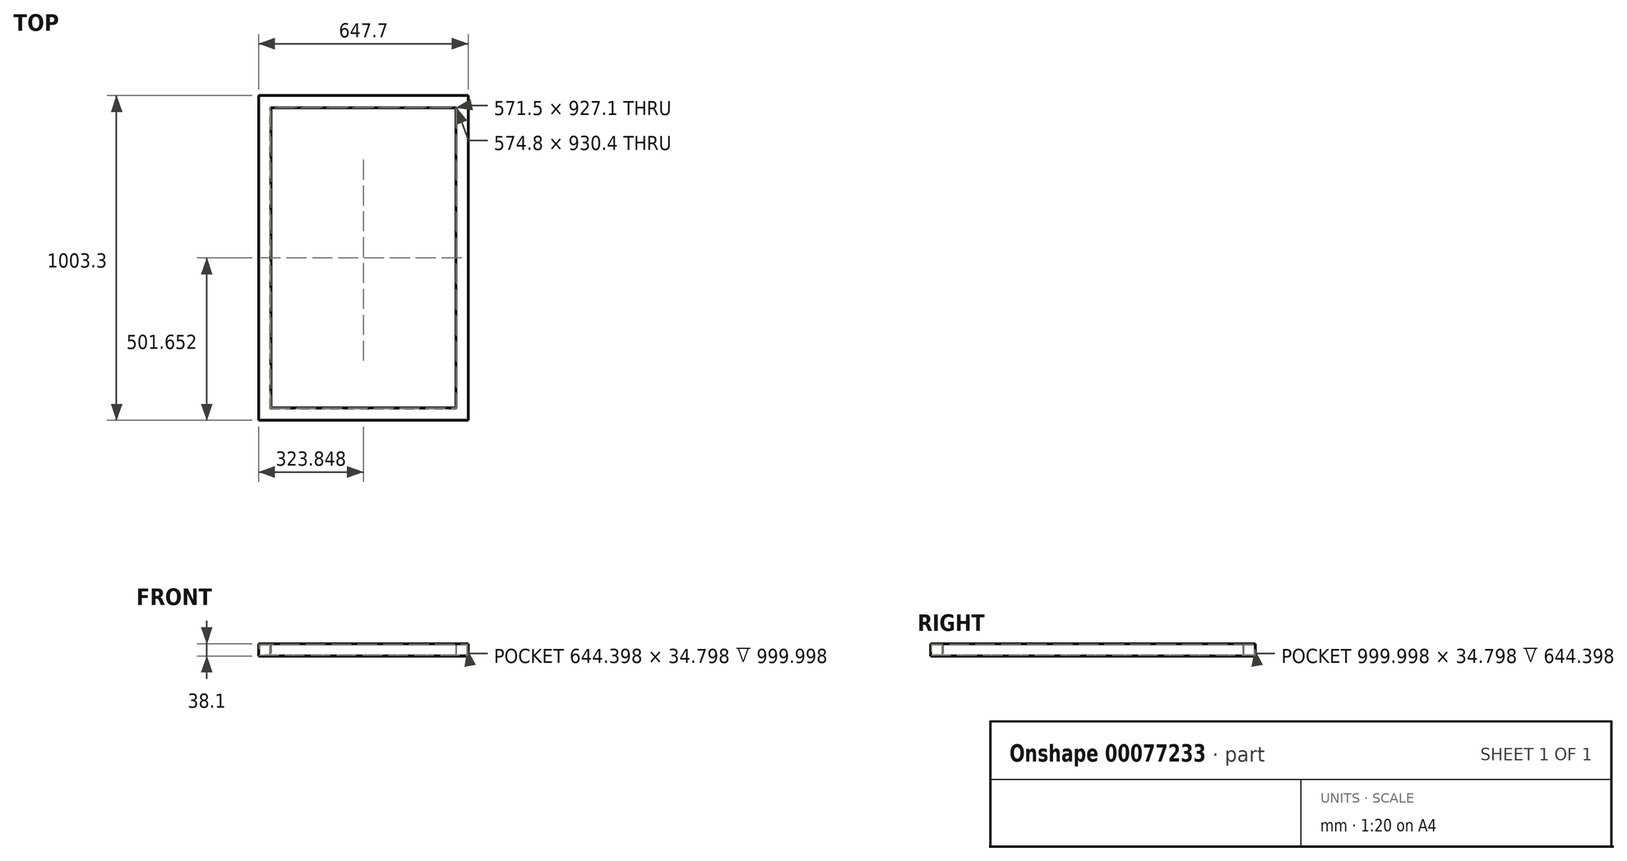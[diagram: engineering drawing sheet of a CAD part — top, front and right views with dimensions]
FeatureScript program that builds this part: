
annotation { "Feature Type Name" : "Feature", "Feature Type Description" : "" }
export const myFeature = defineFeature(function(context is Context, id is Id, definition is map)
    precondition{}
    {
        {
            var Q0;
            Q0=qCreatedBy(makeId("Top.planeOp"),FACE);
            var sketch = newSketch(context, id + "F0", { "sketchPlane" : qUnion([Q0])});
            skLineSegment(sketch, "E0", {"start": v(-90.31, 507.3) * mm, "end": v(-90.31, -496) * mm});
            skLineSegment(sketch, "E1", {"start": v(-90.31, -496) * mm, "end": v(-52.21, -457.9) * mm});
            skLineSegment(sketch, "E2", {"start": v(-52.21, -457.9) * mm, "end": v(-52.21, 469.2) * mm});
            skLineSegment(sketch, "E3", {"start": v(-52.21, 469.2) * mm, "end": v(-90.31, 507.3) * mm});
            skLineSegment(sketch, "E4", {"start": v(-90.31, 507.3) * mm, "end": v(557.39, 507.3) * mm});
            skLineSegment(sketch, "E5", {"start": v(-52.21, 469.2) * mm, "end": v(519.29, 469.2) * mm});
            skLineSegment(sketch, "E6", {"start": v(519.29, 469.2) * mm, "end": v(557.39, 507.3) * mm});
            skLineSegment(sketch, "E7", {"start": v(519.29, 469.2) * mm, "end": v(519.29, -457.9) * mm});
            skLineSegment(sketch, "E8", {"start": v(557.39, 507.3) * mm, "end": v(557.39, -496) * mm});
            skLineSegment(sketch, "E9", {"start": v(557.39, -496) * mm, "end": v(519.29, -457.9) * mm});
            skLineSegment(sketch, "E10", {"start": v(-90.31, -496) * mm, "end": v(557.39, -496) * mm});
            skLineSegment(sketch, "E11", {"start": v(519.29, -457.9) * mm, "end": v(-52.21, -457.9) * mm});
            skSolve(sketch);
        }
        {
            var Q0;
            Q0=makeQuery(id+"F0.imprint","IMPRINT",FACE,{"disambiguationData":[TD([[makeQuery(id+"F0.imprint","IMPRINT",EDGE,{"derivedFrom":sQuery(id+"F0.wireOp",EDGE,"E0")}),1.0]])]});
            extrude(context, id + "F1", {"entities" : qUnion([Q0]), "endBound" : BoundingType.SYMMETRIC, "depth" : 38.1 * mm});
        }
        {
            var Q0;
            Q0=qCreatedBy(makeId("Front.planeOp"),FACE);
            var sketch = newSketch(context, id + "F2", { "sketchPlane" : qUnion([Q0])});
            skLineSegment(sketch, "E12.bottom", {"start": v(-88.66, 17.4) * mm, "end": v(-53.86, 17.4) * mm});
            skLineSegment(sketch, "E12.top", {"start": v(-88.66, -17.4) * mm, "end": v(-53.86, -17.4) * mm});
            skLineSegment(sketch, "E12.left", {"start": v(-88.66, 17.4) * mm, "end": v(-88.66, -17.4) * mm});
            skLineSegment(sketch, "E12.right", {"start": v(-53.86, 17.4) * mm, "end": v(-53.86, -17.4) * mm});
            skSolve(sketch);
        }
        {
            var Q0;
            Q0 = qSketchRegion(id + "F2", true);
            extrude(context, id + "F3", {"entities" : qUnion([Q0]), "operationType" : NewBodyOperationType.REMOVE, "endBound" : BoundingType.SYMMETRIC, "depth" : 1016 * mm});
        }
        {
            var Q0;
            Q0=makeQuery(id+"F0.imprint","IMPRINT",FACE,{"disambiguationData":[TD([[makeQuery(id+"F0.imprint","IMPRINT",EDGE,{"derivedFrom":sQuery(id+"F0.wireOp",EDGE,"E3")}),-1.0]])]});
            extrude(context, id + "F4", {"entities" : qUnion([Q0]), "operationType" : NewBodyOperationType.ADD, "endBound" : BoundingType.SYMMETRIC, "depth" : 38.1 * mm});
        }
        {
            var Q0;
            Q0=qCreatedBy(makeId("Right.planeOp"),FACE);
            var sketch = newSketch(context, id + "F5", { "sketchPlane" : qUnion([Q0])});
            skLineSegment(sketch, "E13.bottom", {"start": v(505.65, 17.4) * mm, "end": v(470.85, 17.4) * mm});
            skLineSegment(sketch, "E13.top", {"start": v(505.65, -17.4) * mm, "end": v(470.85, -17.4) * mm});
            skLineSegment(sketch, "E13.left", {"start": v(505.65, 17.4) * mm, "end": v(505.65, -17.4) * mm});
            skLineSegment(sketch, "E13.right", {"start": v(470.85, 17.4) * mm, "end": v(470.85, -17.4) * mm});
            skPoint(sketch, "E13.middle", {"position": v(488.25, 0) * mm});
            skSolve(sketch);
        }
        {
            var Q0;
            Q0 = qSketchRegion(id + "F5", true);
            var Q1;
            Q1=makeQuery(id+"F1.opExtrude","SWEPT_FACE",FACE,{"disambiguationData":[OSD([sQuery(id+"F0.wireOp",EDGE,"E0")])]});
            var Q2;
            Q2=makeQuery(id+"F4.opExtrude","SWEPT_FACE",FACE,{"disambiguationData":[OSD([sQuery(id+"F0.wireOp",EDGE,"E4")])]});
            extrude(context, id + "F6", {"entities" : qUnion([Q0]), "operationType" : NewBodyOperationType.REMOVE, "endBound" : BoundingType.UP_TO_NEXT, "endBoundEntityFace" : qUnion([Q1]), "depth" : 610.27 * mm, "hasSecondDirection" : true, "secondDirectionBound" : SecondDirectionBoundingType.UP_TO_NEXT, "secondDirectionOppositeDirection" : true, "secondDirectionBoundEntityFace" : qUnion([Q2]), "secondDirectionDepth" : 25.4 * mm});
        }
        {
            var Q0;
            Q0=makeQuery(id+"F0.imprint","IMPRINT",FACE,{"disambiguationData":[TD([[makeQuery(id+"F0.imprint","IMPRINT",EDGE,{"derivedFrom":sQuery(id+"F0.wireOp",EDGE,"E6")}),-1.0]])]});
            var Q1;
            Q1 = qSketchRegion(id + "F8", true);
            extrude(context, id + "F7", {"entities" : qUnion([Q0, Q1]), "operationType" : NewBodyOperationType.ADD, "endBound" : BoundingType.SYMMETRIC, "depth" : 38.1 * mm});
        }
        {
            var Q0;
            Q0=qCreatedBy(makeId("Front.planeOp"),FACE);
            var sketch = newSketch(context, id + "F8", { "sketchPlane" : qUnion([Q0])});
            skLineSegment(sketch, "E14.bottom", {"start": v(555.74, 17.4) * mm, "end": v(520.94, 17.4) * mm});
            skLineSegment(sketch, "E14.top", {"start": v(555.74, -17.4) * mm, "end": v(520.94, -17.4) * mm});
            skLineSegment(sketch, "E14.left", {"start": v(555.74, 17.4) * mm, "end": v(555.74, -17.4) * mm});
            skLineSegment(sketch, "E14.right", {"start": v(520.94, 17.4) * mm, "end": v(520.94, -17.4) * mm});
            skSolve(sketch);
        }
        {
            var Q0;
            Q0 = qSketchRegion(id + "F8", true);
            var Q1;
            Q1=makeQuery(id+"F4.opExtrude","SWEPT_FACE",FACE,{"disambiguationData":[OSD([sQuery(id+"F0.wireOp",EDGE,"E5")])]});
            var Q2;
            Q2=makeQuery(id+"F1.opExtrude","SWEPT_BODY",BODY,{"disambiguationData":[OSD([sQuery(id+"F0.wireOp",EDGE,"E0"),sQuery(id+"F0.wireOp",EDGE,"E1"),sQuery(id+"F0.wireOp",EDGE,"E2"),sQuery(id+"F0.wireOp",EDGE,"E3")])]});
            var Q3;
            Q3=makeQuery(id+"F1.opExtrude","SWEPT_BODY",BODY,{"disambiguationData":[OSD([sQuery(id+"F0.wireOp",EDGE,"E0"),sQuery(id+"F0.wireOp",EDGE,"E1"),sQuery(id+"F0.wireOp",EDGE,"E2"),sQuery(id+"F0.wireOp",EDGE,"E3")])]});
            extrude(context, id + "F9", {"entities" : qUnion([Q0]), "operationType" : NewBodyOperationType.REMOVE, "endBound" : BoundingType.UP_TO_BODY, "oppositeDirection" : true, "endBoundEntityFace" : qUnion([Q1]), "endBoundEntityBody" : qUnion([Q2]), "depth" : 25.4 * mm, "hasSecondDirection" : true, "secondDirectionBound" : SecondDirectionBoundingType.UP_TO_BODY, "secondDirectionOppositeDirection" : false, "secondDirectionBoundEntityBody" : qUnion([Q3]), "secondDirectionDepth" : 25.4 * mm});
        }
        {
            var Q0;
            Q0=makeQuery(id+"F0.imprint","IMPRINT",FACE,{"disambiguationData":[TD([[makeQuery(id+"F0.imprint","IMPRINT",EDGE,{"derivedFrom":sQuery(id+"F0.wireOp",EDGE,"E1")}),-1.0]])]});
            extrude(context, id + "F10", {"entities" : qUnion([Q0]), "operationType" : NewBodyOperationType.ADD, "endBound" : BoundingType.SYMMETRIC, "depth" : 38.1 * mm});
        }
        {
            var Q0;
            Q0=qCreatedBy(makeId("Right.planeOp"),FACE);
            var sketch = newSketch(context, id + "F11", { "sketchPlane" : qUnion([Q0])});
            skLineSegment(sketch, "E15.bottom", {"start": v(-494.35, 17.4) * mm, "end": v(-459.55, 17.4) * mm});
            skLineSegment(sketch, "E15.top", {"start": v(-494.35, -17.4) * mm, "end": v(-459.55, -17.4) * mm});
            skLineSegment(sketch, "E15.left", {"start": v(-494.35, 17.4) * mm, "end": v(-494.35, -17.4) * mm});
            skLineSegment(sketch, "E15.right", {"start": v(-459.55, 17.4) * mm, "end": v(-459.55, -17.4) * mm});
            skSolve(sketch);
        }
        {
            var Q0;
            Q0 = qSketchRegion(id + "F11", true);
            var Q1;
            Q1=makeQuery(id+"F1.opExtrude","SWEPT_BODY",BODY,{"disambiguationData":[OSD([sQuery(id+"F0.wireOp",EDGE,"E0"),sQuery(id+"F0.wireOp",EDGE,"E1"),sQuery(id+"F0.wireOp",EDGE,"E2"),sQuery(id+"F0.wireOp",EDGE,"E3")])]});
            var Q2;
            Q2=makeQuery(id+"F1.opExtrude","SWEPT_BODY",BODY,{"disambiguationData":[OSD([sQuery(id+"F0.wireOp",EDGE,"E0"),sQuery(id+"F0.wireOp",EDGE,"E1"),sQuery(id+"F0.wireOp",EDGE,"E2"),sQuery(id+"F0.wireOp",EDGE,"E3")])]});
            extrude(context, id + "F12", {"entities" : qUnion([Q0]), "operationType" : NewBodyOperationType.REMOVE, "endBound" : BoundingType.UP_TO_BODY, "oppositeDirection" : true, "endBoundEntityBody" : qUnion([Q1]), "depth" : 25.4 * mm, "hasSecondDirection" : true, "secondDirectionBound" : SecondDirectionBoundingType.UP_TO_BODY, "secondDirectionOppositeDirection" : false, "secondDirectionBoundEntityBody" : qUnion([Q2]), "secondDirectionDepth" : 25.4 * mm});
        }
    });
